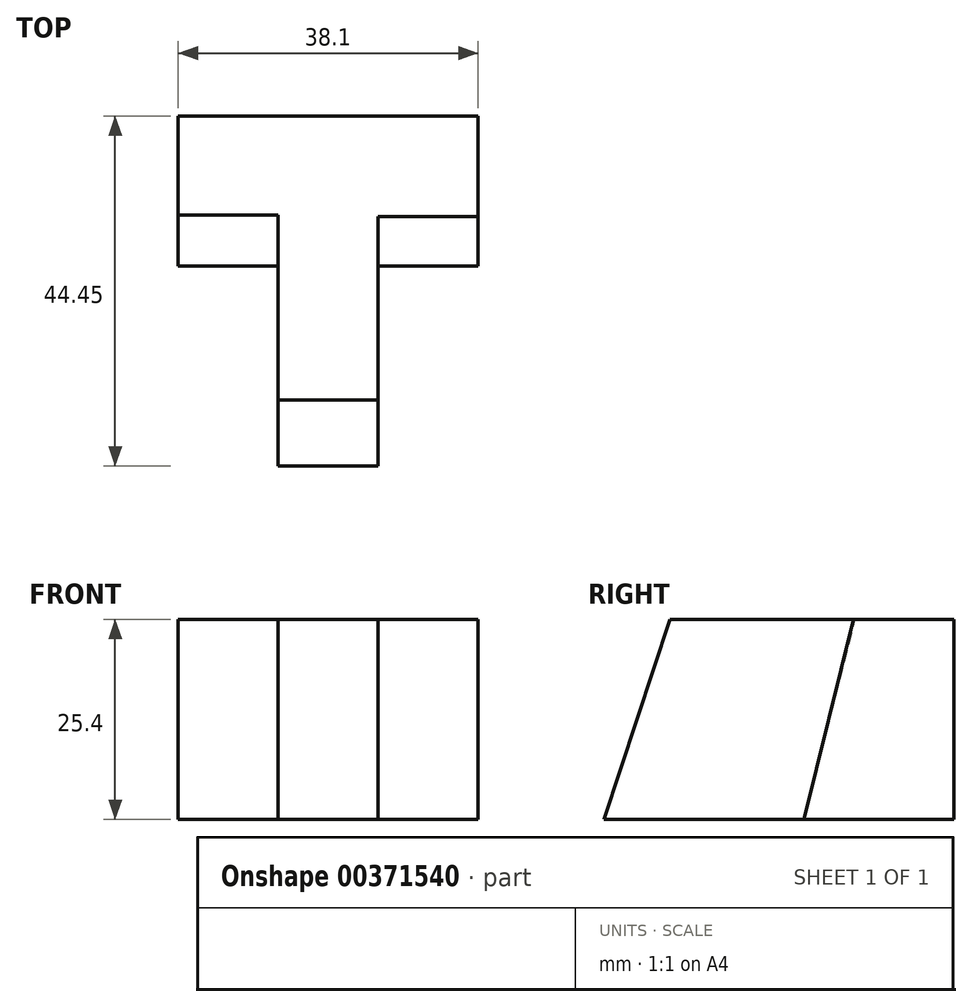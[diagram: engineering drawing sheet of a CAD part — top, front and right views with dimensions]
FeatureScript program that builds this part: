
annotation { "Feature Type Name" : "Feature", "Feature Type Description" : "" }
export const myFeature = defineFeature(function(context is Context, id is Id, definition is map)
    precondition{}
    {
        {
            var Q0;
            Q0=qCreatedBy(makeId("Top.planeOp"),FACE);
            var sketch = newSketch(context, id + "F0", { "sketchPlane" : qUnion([Q0])});
            skLineSegment(sketch, "E0", {"start": v(0, 0) * mm, "end": v(12.7, 0) * mm});
            skLineSegment(sketch, "E1", {"start": v(12.7, 0) * mm, "end": v(12.7, 25.4) * mm});
            skLineSegment(sketch, "E2", {"start": v(12.7, 25.4) * mm, "end": v(25.4, 25.4) * mm});
            skLineSegment(sketch, "E3", {"start": v(25.4, 25.4) * mm, "end": v(25.4, 44.45) * mm});
            skLineSegment(sketch, "E4", {"start": v(25.4, 44.45) * mm, "end": v(-12.7, 44.45) * mm});
            skLineSegment(sketch, "E5", {"start": v(-12.7, 44.45) * mm, "end": v(-12.7, 25.4) * mm});
            skLineSegment(sketch, "E6", {"start": v(-12.7, 25.4) * mm, "end": v(0, 25.4) * mm});
            skLineSegment(sketch, "E7", {"start": v(0, 25.4) * mm, "end": v(0, 0) * mm});
            skSolve(sketch);
        }
        {
            var Q0;
            Q0=makeQuery(id+"F0.imprint","IMPRINT",FACE,{"disambiguationData":[TD([[makeQuery(id+"F0.imprint","IMPRINT",EDGE,{"derivedFrom":sQuery(id+"F0.wireOp",EDGE,"E0")}),1.0]])]});
            extrude(context, id + "F1", {"entities" : qUnion([Q0]), "depth" : 25.4 * mm});
        }
        {
            var Q0;
            Q0=makeQuery(id+"F1.opExtrude","SWEPT_FACE",FACE,{"disambiguationData":[OSD([sQuery(id+"F0.wireOp",EDGE,"E7")])]});
            var sketch = newSketch(context, id + "F2", { "sketchPlane" : qUnion([Q0])});
            skLineSegment(sketch, "E8", {"start": v(0, 0) * mm, "end": v(-8.36, 25.4) * mm});
            skSolve(sketch);
        }
        {
            var Q0;
            Q0 = qSketchRegion(id + "F2", true);
            var Q1;
            {var subQ0=sQuery(id+"F2.wireOp",EDGE,"E8");Q1=makeQuery(id+"F2.imprint","IMPRINT",FACE,{"disambiguationData":[TD([[makeQuery(id+"F2.imprint","IMPRINT",EDGE,{"derivedFrom":subQ0}),-1.0]])]});}
            extrude(context, id + "F3", {"entities" : qUnion([Q0, Q1]), "operationType" : NewBodyOperationType.REMOVE, "oppositeDirection" : true, "depth" : 25.4 * mm});
        }
        {
            var Q0;
            Q0=makeQuery(id+"F1.opExtrude","SWEPT_FACE",FACE,{"disambiguationData":[OSD([sQuery(id+"F0.wireOp",EDGE,"E5")])]});
            var sketch = newSketch(context, id + "F4", { "sketchPlane" : qUnion([Q0])});
            skLineSegment(sketch, "E9", {"start": v(-25.4, 0) * mm, "end": v(-31.88, 25.4) * mm});
            skSolve(sketch);
        }
        {
            var Q0;
            Q0=makeQuery(id+"F1.opExtrude","SWEPT_FACE",FACE,{"disambiguationData":[OSD([sQuery(id+"F0.wireOp",EDGE,"E3")])]});
            var sketch = newSketch(context, id + "F5", { "sketchPlane" : qUnion([Q0])});
            skLineSegment(sketch, "E10", {"start": v(31.67, 25.4) * mm, "end": v(25.4, 0) * mm});
            skSolve(sketch);
        }
        {
            var Q0;
            Q0 = qSketchRegion(id + "F5", true);
            var Q1;
            {var subQ0=sQuery(id+"F5.wireOp",EDGE,"E10");Q1=makeQuery(id+"F5.imprint","IMPRINT",FACE,{"disambiguationData":[TD([[makeQuery(id+"F5.imprint","IMPRINT",EDGE,{"derivedFrom":subQ0}),-1.0]])]});}
            extrude(context, id + "F6", {"entities" : qUnion([Q0, Q1]), "operationType" : NewBodyOperationType.REMOVE, "oppositeDirection" : true, "depth" : 12.7 * mm});
        }
        {
            var Q0;
            {var subQ0=sQuery(id+"F4.wireOp",EDGE,"E9");Q0=makeQuery(id+"F4.imprint","IMPRINT",FACE,{"disambiguationData":[TD([[makeQuery(id+"F4.imprint","IMPRINT",EDGE,{"derivedFrom":subQ0}),-1.0]])]});}
            extrude(context, id + "F7", {"entities" : qUnion([Q0]), "operationType" : NewBodyOperationType.REMOVE, "oppositeDirection" : true, "depth" : 12.7 * mm});
        }
    });
